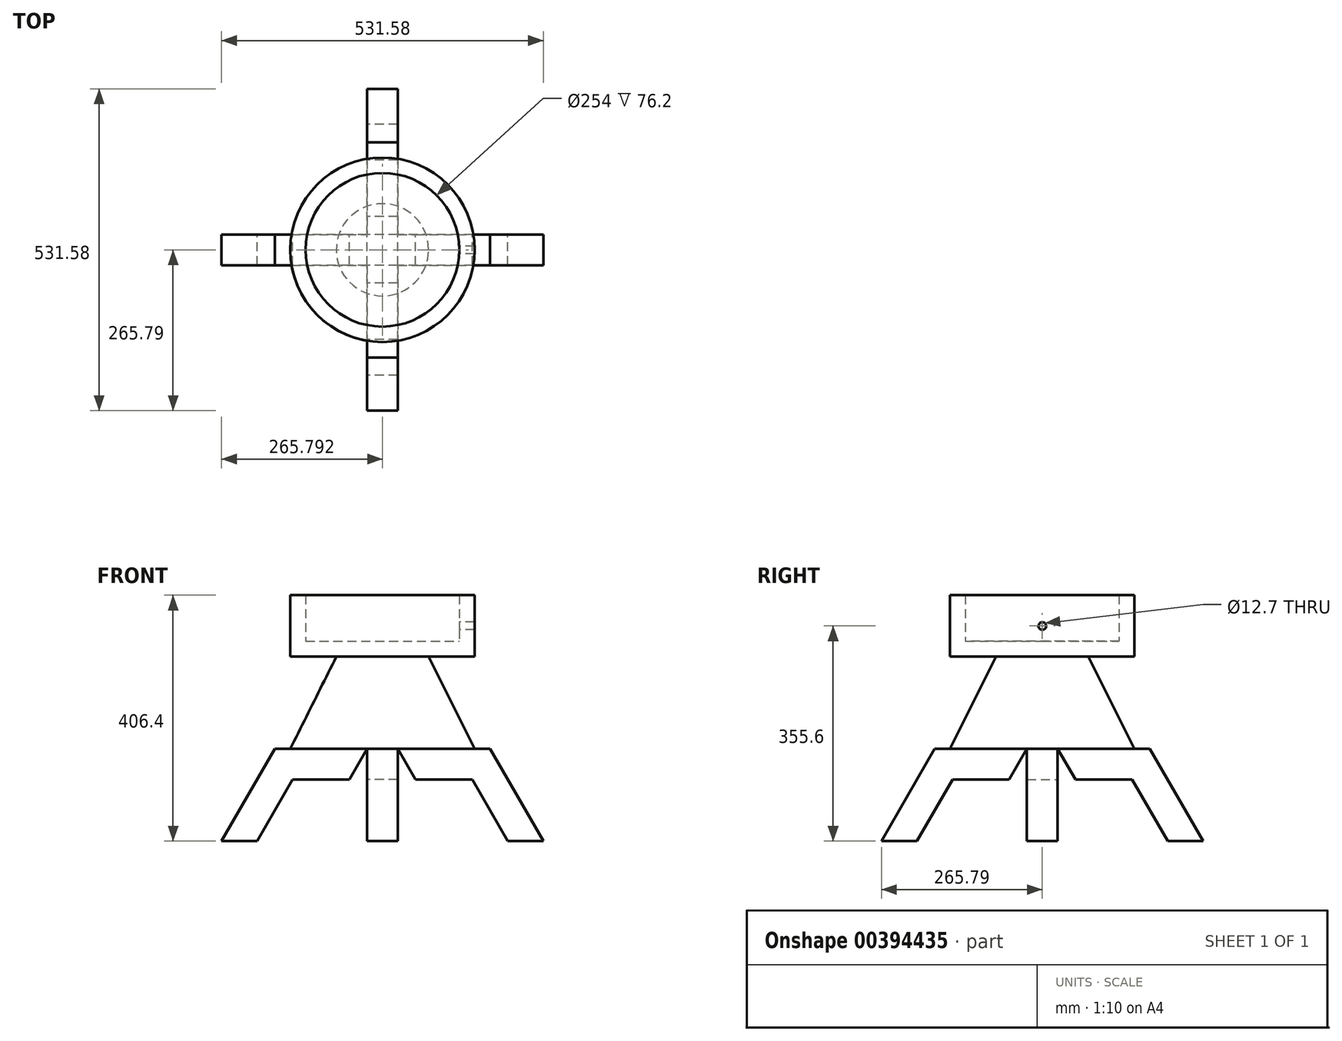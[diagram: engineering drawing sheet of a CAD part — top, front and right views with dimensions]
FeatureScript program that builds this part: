
annotation { "Feature Type Name" : "Feature", "Feature Type Description" : "" }
export const myFeature = defineFeature(function(context is Context, id is Id, definition is map)
    precondition{}
    {
        {
            var Q0;
            Q0=qCreatedBy(makeId("Front.planeOp"),FACE);
            var sketch = newSketch(context, id + "F0", { "sketchPlane" : qUnion([Q0])});
            skLineSegment(sketch, "E0", {"start": v(0, 0) * mm, "end": v(-87.99, 152.4) * mm});
            skLineSegment(sketch, "E1", {"start": v(-87.99, 152.4) * mm, "end": v(-240.39, 152.4) * mm});
            skLineSegment(sketch, "E2", {"start": v(-240.39, 152.4) * mm, "end": v(-211.06, 101.6) * mm});
            skLineSegment(sketch, "E3", {"start": v(-211.06, 101.6) * mm, "end": v(-117.32, 101.6) * mm});
            skLineSegment(sketch, "E4", {"start": v(-117.32, 101.6) * mm, "end": v(-58.66, 0) * mm});
            skLineSegment(sketch, "E5", {"start": v(-58.66, 0) * mm, "end": v(0, 0) * mm});
            skLineSegment(sketch, "E6", {"start": v(-240.39, 152.4) * mm, "end": v(-291.19, 152.4) * mm});
            skLineSegment(sketch, "E7", {"start": v(-291.19, 152.4) * mm, "end": v(-320.52, 101.6) * mm});
            skLineSegment(sketch, "E8", {"start": v(-320.52, 101.6) * mm, "end": v(-414.26, 101.6) * mm});
            skLineSegment(sketch, "E9", {"start": v(-414.26, 101.6) * mm, "end": v(-472.92, 0) * mm});
            skLineSegment(sketch, "E10", {"start": v(-472.92, 0) * mm, "end": v(-531.58, 0) * mm});
            skLineSegment(sketch, "E11", {"start": v(-531.58, 0) * mm, "end": v(-443.59, 152.4) * mm});
            skLineSegment(sketch, "E12", {"start": v(-443.59, 152.4) * mm, "end": v(-291.19, 152.4) * mm});
            skSolve(sketch);
        }
        {
            var Q0;
            Q0=makeQuery(id+"F0.imprint","IMPRINT",FACE,{"disambiguationData":[TD([[makeQuery(id+"F0.imprint","IMPRINT",EDGE,{"derivedFrom":sQuery(id+"F0.wireOp",EDGE,"E7")}),-1.0]])]});
            var Q1;
            Q1=makeQuery(id+"F0.imprint","IMPRINT",FACE,{"disambiguationData":[TD([[makeQuery(id+"F0.imprint","IMPRINT",EDGE,{"derivedFrom":sQuery(id+"F0.wireOp",EDGE,"E0")}),1.0]])]});
            extrude(context, id + "F1", {"entities" : qUnion([Q0, Q1]), "depth" : 50.8 * mm});
        }
        {
            var Q0;
            Q0=makeQuery(id+"F1.opExtrude","SWEPT_FACE",FACE,{"disambiguationData":[OSD([sQuery(id+"F0.wireOp",EDGE,"E7")])]});
            var Q1;
            Q1=makeQuery(id+"F1.opExtrude","SWEPT_EDGE",EDGE,{"disambiguationData":[OSD([sQuery(id+"F0.wireOp",EDGE,"E7"),sQuery(id+"F0.wireOp",EDGE,"E12")])]});
            cPlane(context, id + "F2", {"entities" : qUnion([Q0, Q1]), "cplaneType" : CPlaneType.LINE_ANGLE, "offset" : 25.4 * mm, "angle" : 30 * degree, "oppositeDirection" : true, "width" : 152.4 * mm, "height" : 152.4 * mm});
        }
        {
            var Q0;
            Q0=qCreatedBy(id+"F2.planeOp",FACE);
            var sketch = newSketch(context, id + "F3", { "sketchPlane" : qUnion([Q0])});
            skLineSegment(sketch, "E13.0", {"start": v(0, 152.4) * mm, "end": v(0, 101.6) * mm});
            skLineSegment(sketch, "E14.0.0", {"start": v(0, 101.6) * mm, "end": v(0, 152.4) * mm});
            skLineSegment(sketch, "E14.0.1", {"start": v(0, 152.4) * mm, "end": v(50.8, 152.4) * mm});
            skLineSegment(sketch, "E14.0.2", {"start": v(50.8, 152.4) * mm, "end": v(50.8, 101.6) * mm});
            skLineSegment(sketch, "E14.0.3", {"start": v(50.8, 101.6) * mm, "end": v(0, 101.6) * mm});
            skLineSegment(sketch, "E15", {"start": v(0, 152.4) * mm, "end": v(-152.4, 152.4) * mm});
            skLineSegment(sketch, "E16", {"start": v(-152.4, 152.4) * mm, "end": v(-240.39, 0) * mm});
            skLineSegment(sketch, "E17", {"start": v(-240.39, 0) * mm, "end": v(-181.73, 0) * mm});
            skLineSegment(sketch, "E18", {"start": v(-181.73, 0) * mm, "end": v(-123.07, 101.6) * mm});
            skLineSegment(sketch, "E19", {"start": v(-123.07, 101.6) * mm, "end": v(-29.33, 101.6) * mm});
            skLineSegment(sketch, "E20", {"start": v(-29.33, 101.6) * mm, "end": v(0, 152.4) * mm});
            skLineSegment(sketch, "E21", {"start": v(50.8, 152.4) * mm, "end": v(203.2, 152.4) * mm});
            skLineSegment(sketch, "E22", {"start": v(203.2, 152.4) * mm, "end": v(291.19, 0) * mm});
            skLineSegment(sketch, "E23", {"start": v(291.19, 0) * mm, "end": v(232.53, 0) * mm});
            skLineSegment(sketch, "E24", {"start": v(232.53, 0) * mm, "end": v(173.87, 101.6) * mm});
            skLineSegment(sketch, "E25", {"start": v(173.87, 101.6) * mm, "end": v(80.13, 101.6) * mm});
            skLineSegment(sketch, "E26", {"start": v(80.13, 101.6) * mm, "end": v(50.8, 152.4) * mm});
            skSolve(sketch);
        }
        {
            var Q0;
            Q0=makeQuery(id+"F3.imprint","IMPRINT",FACE,{"disambiguationData":[TD([[makeQuery(id+"F3.imprint","IMPRINT",EDGE,{"derivedFrom":sQuery(id+"F3.wireOp",EDGE,"E21")}),-1.0]])]});
            var Q1;
            Q1=makeQuery(id+"F3.imprint","IMPRINT",FACE,{"disambiguationData":[TD([[makeQuery(id+"F3.imprint","IMPRINT",EDGE,{"derivedFrom":sQuery(id+"F3.wireOp",EDGE,"E15")}),1.0]])]});
            extrude(context, id + "F4", {"entities" : qUnion([Q0, Q1]), "oppositeDirection" : true, "depth" : 50.8 * mm});
        }
        {
            var Q0;
            Q0=makeQuery(id+"F4.opExtrude","SWEPT_FACE",FACE,{"disambiguationData":[OSD([sQuery(id+"F3.wireOp",EDGE,"E21")])]});
            var sketch = newSketch(context, id + "F5", { "sketchPlane" : qUnion([Q0])});
            skLineSegment(sketch, "E27.0.0", {"start": v(-291.19, -50.8) * mm, "end": v(-291.19, -203.2) * mm});
            skLineSegment(sketch, "E27.0.1", {"start": v(-291.19, -203.2) * mm, "end": v(-240.39, -203.2) * mm});
            skLineSegment(sketch, "E27.0.2", {"start": v(-240.39, -203.2) * mm, "end": v(-240.39, -50.8) * mm});
            skLineSegment(sketch, "E27.0.3", {"start": v(-240.39, -50.8) * mm, "end": v(-291.19, -50.8) * mm});
            skLineSegment(sketch, "E28.0.0", {"start": v(-291.19, 0) * mm, "end": v(-443.59, 0) * mm});
            skLineSegment(sketch, "E28.0.1", {"start": v(-443.59, 0) * mm, "end": v(-443.59, -50.8) * mm});
            skLineSegment(sketch, "E28.0.2", {"start": v(-443.59, -50.8) * mm, "end": v(-291.19, -50.8) * mm});
            skLineSegment(sketch, "E28.0.3", {"start": v(-291.19, -50.8) * mm, "end": v(-291.19, 0) * mm});
            skLineSegment(sketch, "E29.0.0", {"start": v(-87.99, 0) * mm, "end": v(-240.39, 0) * mm});
            skLineSegment(sketch, "E29.0.1", {"start": v(-240.39, 0) * mm, "end": v(-240.39, -50.8) * mm});
            skLineSegment(sketch, "E29.0.2", {"start": v(-240.39, -50.8) * mm, "end": v(-87.99, -50.8) * mm});
            skLineSegment(sketch, "E29.0.3", {"start": v(-87.99, -50.8) * mm, "end": v(-87.99, 0) * mm});
            skLineSegment(sketch, "E30.0.0", {"start": v(-291.19, 152.4) * mm, "end": v(-291.19, 0) * mm});
            skLineSegment(sketch, "E30.0.1", {"start": v(-291.19, 0) * mm, "end": v(-240.39, 0) * mm});
            skLineSegment(sketch, "E30.0.2", {"start": v(-240.39, 0) * mm, "end": v(-240.39, 152.4) * mm});
            skLineSegment(sketch, "E30.0.3", {"start": v(-240.39, 152.4) * mm, "end": v(-291.19, 152.4) * mm});
            skLineSegment(sketch, "E31", {"start": v(-291.19, -50.8) * mm, "end": v(-240.39, 0) * mm});
            skLineSegment(sketch, "E32", {"start": v(-291.19, 0) * mm, "end": v(-240.39, -50.8) * mm});
            skCircle(sketch, "E33", {"center": v(-265.79, -25.4) * mm, "radius": 152.4 * mm});
            skSolve(sketch);
        }
        {
            var Q0;
            Q0=qCreatedBy(id+"F2.planeOp",FACE);
            cPlane(context, id + "F6", {"entities" : qUnion([Q0]), "cplaneType" : CPlaneType.OFFSET, "offset" : 25.4 * mm, "oppositeDirection" : true, "width" : 152.4 * mm, "height" : 152.4 * mm});
        }
        {
            var Q0;
            Q0=qCreatedBy(id+"F6.planeOp",FACE);
            var sketch = newSketch(context, id + "F7", { "sketchPlane" : qUnion([Q0])});
            skPoint(sketch, "E34.0", {"position": v(25.4, 152.4) * mm});
            skLineSegment(sketch, "E35", {"start": v(25.4, 152.4) * mm, "end": v(25.4, 304.8) * mm});
            skLineSegment(sketch, "E36", {"start": v(25.4, 304.8) * mm, "end": v(101.6, 304.8) * mm});
            skLineSegment(sketch, "E37", {"start": v(101.6, 304.8) * mm, "end": v(177.8, 152.4) * mm});
            skLineSegment(sketch, "E38", {"start": v(177.8, 152.4) * mm, "end": v(25.4, 152.4) * mm});
            skLineSegment(sketch, "E39", {"start": v(25.4, 304.8) * mm, "end": v(177.8, 304.8) * mm});
            skLineSegment(sketch, "E40", {"start": v(177.8, 304.8) * mm, "end": v(177.8, 406.4) * mm});
            skLineSegment(sketch, "E41", {"start": v(25.4, 304.8) * mm, "end": v(25.4, 355.6) * mm});
            skCircle(sketch, "E42", {"center": v(25.4, 355.6) * mm, "radius": 6.35 * mm});
            skLineSegment(sketch, "E43", {"start": v(177.8, 406.4) * mm, "end": v(152.4, 406.4) * mm});
            skLineSegment(sketch, "E44", {"start": v(152.4, 406.4) * mm, "end": v(152.4, 330.2) * mm});
            skLineSegment(sketch, "E45", {"start": v(152.4, 330.2) * mm, "end": v(25.4, 330.2) * mm});
            skSolve(sketch);
        }
        {
            var Q0;
            {var subQ0=sQuery(id+"F5.wireOp",EDGE,"E27.0.3");Q0=makeQuery(id+"F5.imprint","IMPRINT",FACE,{"disambiguationData":[TD([[makeQuery(id+"F5.imprint","IMPRINT",EDGE,{"derivedFrom":subQ0}),1.0]])]});}
            cPlane(context, id + "F8", {"entities" : qUnion([Q0]), "cplaneType" : CPlaneType.OFFSET, "offset" : 152.4 * mm, "width" : 152.4 * mm, "height" : 152.4 * mm});
        }
        {
            var Q0;
            Q0=makeQuery(id+"F7.imprint","IMPRINT",FACE,{"disambiguationData":[TD([[makeQuery(id+"F7.imprint","IMPRINT",EDGE,{"derivedFrom":sQuery(id+"F7.wireOp",EDGE,"E35")}),-1.0]])]});
            var Q1;
            Q1=sQuery(id+"F7.wireOp",EDGE,"E35");
            revolve(context, id + "F9", {"operationType" : NewBodyOperationType.ADD, "entities" : qUnion([Q0]), "axis" : qUnion([Q1]), "revolveType" : RevolveType.FULL});
        }
        {
            var Q0;
            {var subQ4=sQuery(id+"F7.wireOp",EDGE,"E40");Q0=makeQuery(id+"F7.imprint","IMPRINT",FACE,{"disambiguationData":[TD([[makeQuery(id+"F7.imprint","IMPRINT",EDGE,{"derivedFrom":subQ4}),1.0]])]});}
            var Q1;
            Q1=sQuery(id+"F7.wireOp",EDGE,"E41");
            revolve(context, id + "F10", {"operationType" : NewBodyOperationType.ADD, "entities" : qUnion([Q0]), "axis" : qUnion([Q1]), "revolveType" : RevolveType.FULL});
        }
        {
            var Q0;
            Q0=makeQuery(id+"F7.imprint","IMPRINT",FACE,{"disambiguationData":[TD([[makeQuery(id+"F7.imprint","IMPRINT",EDGE,{"derivedFrom":sQuery(id+"F7.wireOp",EDGE,"E42")}),1.0]])]});
            extrude(context, id + "F11", {"entities" : qUnion([Q0]), "operationType" : NewBodyOperationType.REMOVE, "oppositeDirection" : true, "depth" : 762 * mm});
        }
    });
